# Revit family: SQN-D
name_source: partatom
category: Mechanical Equipment
revit_build: Autodesk Revit 2016 (Build: 20190507_1515(x64)
units: mm (PartAtom-declared; Revit-internal decimal feet)

## family parameters
Always vertical = Yes
Cut with Voids When Loaded = No
Part Type = Normal
Room Calculation Point = No
Round Connector Dimension = Use Diameter
Shared = No
Work Plane-Based = No

## types (46) — shared parameters
1.5 = 1 1/2"
FLANGE = 1"
HALF_F = 11 1/32"
HALF_G = 11 13/32"
LS = Yes
Manufacturer = Loren Cook Company
ONE EIGTH = 1/8"
T_SQ = 12"
T_SQ_HALF = 6"
URL = www.lorencook.com
ZERO = 0"

## per-type parameters (varying)
- 70_SQN-D: A_SUB=10"; B/2-VF_to_Side=2 13/16"; B_SUB=12"; B_SUB_MIN_.125=11 7/8"; C_SUB=14"; DEPTH=12"; D_PLUS_2=14"; D_SUB=12"; D_SUB_MINUS_.25=11 3/4"; D_SUB_TENTH=1 3/16"; E_SUB=13 9/16"; E_SUB_DIRECT=13 9/16"; FOURTH_B=3"; F_SUB=6 15/16"; G_SUB=6 1/8"; HALFC-B=1"; HALF_2H+D=7"; HALF_B=6"; HALF_B-G=2 15/16"; HALF_D=6"; HALF_D-A=1"; HALF_D-F=2 17/32"; HALF_D_SUB=6"; HALF_D_SUB_MIN_.25=5 7/8"; HALF_MP=2 3/32"; Height_with_VF=29 3/16"; INLET_RADIUS=3"; IN_RAD-D_SUB_TENTH=1 13/16"; IN_TENTH=1 13/16"; MOTOR_DEPTH=-8 3/4"; Model=SQN-D; NEGHALFC-B=-1"; NEG_HALF2H+D=-7"; NEG_HALF_D=-6"; PM=No; RAIL_SPACING=6"; SHAFT_RAD=1 1/8"; TENTHB+FOURTHB=-4 3/16"; TENTH_B=-1 3/16"; Type Comments=Centrifugal Square Inline Direct Drive; VF_to_Rear=2 1/8"; VF_to_Side=3 3/16"
- 90_SQN-D: A_SUB=12"; B/2-VF_to_Side=4 5/16"; B_SUB=15"; B_SUB_MIN_.125=14 7/8"; C_SUB=17"; DEPTH=15"; D_PLUS_2=16"; D_SUB=14"; D_SUB_MINUS_.25=13 3/4"; D_SUB_TENTH=1 13/32"; E_SUB=15 9/16"; E_SUB_DIRECT=15 9/16"; FOURTH_B=3 3/4"; F_SUB=8 15/16"; G_SUB=9 1/8"; HALFC-B=1"; HALF_2H+D=8"; HALF_B=7 1/2"; HALF_B-G=2 15/16"; HALF_D=7"; HALF_D-A=1"; HALF_D-F=2 17/32"; HALF_D_SUB=7"; HALF_D_SUB_MIN_.25=6 7/8"; HALF_MP=2 5/8"; Height_with_VF=29 3/16"; INLET_RADIUS=3 1/2"; IN_RAD-D_SUB_TENTH=2 3/32"; IN_TENTH=2 3/32"; MOTOR_DEPTH=-10 1/4"; Model=SQN-D; NEGHALFC-B=-1"; NEG_HALF2H+D=-8"; NEG_HALF_D=-7"; PM=No; RAIL_SPACING=7 1/2"; SHAFT_RAD=1 5/16"; TENTHB+FOURTHB=-5 1/4"; TENTH_B=-1 1/2"; Type Comments=Centrifugal Square Inline Direct Drive; VF_to_Rear=2 1/8"; VF_to_Side=3 3/16"
- 100_SQN-D: A_SUB=12"; B/2-VF_to_Side=6 13/16"; B_SUB=20"; B_SUB_MIN_.125=19 7/8"; C_SUB=22"; DEPTH=20"; D_PLUS_2=16"; D_SUB=14"; D_SUB_MINUS_.25=13 3/4"; D_SUB_TENTH=1 13/32"; E_SUB=12 1/2"; E_SUB_DIRECT=15 9/16"; FOURTH_B=5"; F_SUB=8 15/16"; G_SUB=14 1/8"; HALFC-B=1"; HALF_2H+D=8"; HALF_B=10"; HALF_B-G=2 15/16"; HALF_D=7"; HALF_D-A=1"; HALF_D-F=2 17/32"; HALF_D_SUB=7"; HALF_D_SUB_MIN_.25=6 7/8"; HALF_MP=3 1/2"; Height_with_VF=29 3/16"; INLET_RADIUS=3 1/2"; IN_RAD-D_SUB_TENTH=2 3/32"; IN_TENTH=2 3/32"; MOTOR_DEPTH=-12 3/4"; Model=SQN-D; NEGHALFC-B=-1"; NEG_HALF2H+D=-8"; NEG_HALF_D=-7"; PM=No; RAIL_SPACING=10"; SHAFT_RAD=1 1/32"; TENTHB+FOURTHB=-7"; TENTH_B=-2"; Type Comments=Centrifugal Square Inline Direct Drive; VF_to_Rear=2 1/8"; VF_to_Side=3 3/16"
- 120_SQN-D: A_SUB=16"; B/2-VF_to_Side=6 13/16"; B_SUB=20"; B_SUB_MIN_.125=19 7/8"; C_SUB=22"; DEPTH=20"; D_PLUS_2=20 7/16"; D_SUB=18 7/16"; D_SUB_MINUS_.25=18 3/16"; D_SUB_TENTH=1 27/32"; E_SUB=12 1/2"; E_SUB_DIRECT=20"; FOURTH_B=5"; F_SUB=12 9/16"; G_SUB=14 1/8"; HALFC-B=1"; HALF_2H+D=10 7/32"; HALF_B=10"; HALF_B-G=2 15/16"; HALF_D=9 7/32"; HALF_D-A=1 7/32"; HALF_D-F=2 15/16"; HALF_D_SUB=9 7/32"; HALF_D_SUB_MIN_.25=9 3/32"; HALF_MP=3 1/2"; Height_with_VF=29 3/16"; INLET_RADIUS=4 5/8"; IN_RAD-D_SUB_TENTH=2 25/32"; IN_TENTH=2 25/32"; MOTOR_DEPTH=-12 3/4"; Model=SQN-D; NEGHALFC-B=-1"; NEG_HALF2H+D=-10 7/32"; NEG_HALF_D=-9 7/32"; PM=No; RAIL_SPACING=10"; SHAFT_RAD=1 1/32"; TENTHB+FOURTHB=-7"; TENTH_B=-2"; Type Comments=Centrifugal Square Inline Direct Drive; VF_to_Rear=2 1/8"; VF_to_Side=3 3/16"
- 135_SQN-D: A_SUB=18"; B/2-VF_to_Side=6 15/16"; B_SUB=20 1/4"; B_SUB_MIN_.125=20 1/8"; C_SUB=22 1/4"; DEPTH=20 1/4"; D_PLUS_2=22 3/4"; D_SUB=20 3/4"; D_SUB_MINUS_.25=20 1/2"; D_SUB_TENTH=2 1/16"; E_SUB=12 1/2"; E_SUB_DIRECT=22 5/16"; FOURTH_B=5 1/16"; F_SUB=13 1/8"; G_SUB=14 1/4"; HALFC-B=1"; HALF_2H+D=11 3/8"; HALF_B=10 1/8"; HALF_B-G=3"; HALF_D=10 3/8"; HALF_D-A=1 3/8"; HALF_D-F=3 13/16"; HALF_D_SUB=10 3/8"; HALF_D_SUB_MIN_.25=10 1/4"; HALF_MP=3 17/32"; Height_with_VF=29 3/16"; INLET_RADIUS=5 3/16"; IN_RAD-D_SUB_TENTH=3 1/8"; IN_TENTH=3 1/8"; MOTOR_DEPTH=-12 7/8"; Model=SQN-D; NEGHALFC-B=-1"; NEG_HALF2H+D=-11 3/8"; NEG_HALF_D=-10 3/8"; PM=No; RAIL_SPACING=10 1/8"; SHAFT_RAD=1 1/32"; TENTHB+FOURTHB=-7 3/32"; TENTH_B=-2 1/32"; Type Comments=Centrifugal Square Inline Direct Drive; VF_to_Rear=2 1/8"; VF_to_Side=3 3/16"
- 150_SQN-D: A_SUB=20"; B/2-VF_to_Side=7 3/4"; B_SUB=21 7/8"; B_SUB_MIN_.125=21 3/4"; C_SUB=23 7/8"; DEPTH=21 7/8"; D_PLUS_2=25"; D_SUB=23"; D_SUB_MINUS_.25=22 3/4"; D_SUB_TENTH=2 5/16"; E_SUB=12 3/4"; E_SUB_DIRECT=25 1/16"; FOURTH_B=5 15/32"; F_SUB=16 1/8"; G_SUB=15 15/16"; HALFC-B=1"; HALF_2H+D=12 1/2"; HALF_B=10 15/16"; HALF_B-G=2 31/32"; HALF_D=11 1/2"; HALF_D-A=1 1/2"; HALF_D-F=3 7/16"; HALF_D_SUB=11 1/2"; HALF_D_SUB_MIN_.25=11 3/8"; HALF_MP=3 27/32"; Height_with_VF=29 3/16"; INLET_RADIUS=5 3/4"; IN_RAD-D_SUB_TENTH=3 7/16"; IN_TENTH=3 7/16"; MOTOR_DEPTH=-13 11/16"; Model=SQN-D; NEGHALFC-B=-1"; NEG_HALF2H+D=-12 1/2"; NEG_HALF_D=-11 1/2"; PM=No; RAIL_SPACING=10 15/16"; SHAFT_RAD=1 1/16"; TENTHB+FOURTHB=-7 21/32"; TENTH_B=-2 3/16"; Type Comments=Centrifugal Square Inline Direct Drive; VF_to_Rear=2 1/8"; VF_to_Side=3 3/16"
- 165_SQN-D: A_SUB=22"; B/2-VF_to_Side=9 5/16"; B_SUB=25"; B_SUB_MIN_.125=24 7/8"; C_SUB=27"; DEPTH=25"; D_PLUS_2=27 5/16"; D_SUB=25 5/16"; D_SUB_MINUS_.25=25 1/16"; D_SUB_TENTH=2 17/32"; E_SUB=14 3/4"; E_SUB_DIRECT=27 3/8"; FOURTH_B=6 1/4"; F_SUB=18 1/8"; G_SUB=19 1/8"; HALFC-B=1"; HALF_2H+D=13 21/32"; HALF_B=12 1/2"; HALF_B-G=2 15/16"; HALF_D=12 21/32"; HALF_D-A=1 21/32"; HALF_D-F=3 19/32"; HALF_D_SUB=12 21/32"; HALF_D_SUB_MIN_.25=12 17/32"; HALF_MP=4 3/8"; Height_with_VF=29 3/16"; INLET_RADIUS=6 11/32"; IN_RAD-D_SUB_TENTH=3 13/16"; IN_TENTH=3 13/16"; MOTOR_DEPTH=-15 1/4"; Model=SQN-D; NEGHALFC-B=-1"; NEG_HALF2H+D=-13 21/32"; NEG_HALF_D=-12 21/32"; PM=No; RAIL_SPACING=12 1/2"; SHAFT_RAD=1 7/32"; TENTHB+FOURTHB=-8 3/4"; TENTH_B=-2 1/2"; Type Comments=Centrifugal Square Inline Direct Drive; VF_to_Rear=2 1/8"; VF_to_Side=3 3/16"
- 120_SQN-D-VF: A_SUB=16"; B/2-VF_to_Side=6 13/16"; B_SUB=20"; B_SUB_MIN_.125=19 7/8"; C_SUB=22"; DEPTH=20"; D_PLUS_2=20 7/16"; D_SUB=18 7/16"; D_SUB_MINUS_.25=18 3/16"; D_SUB_TENTH=1 27/32"; E_SUB=12 1/2"; E_SUB_DIRECT=20"; FOURTH_B=5"; F_SUB=12 9/16"; G_SUB=14 1/8"; HALFC-B=1"; HALF_2H+D=10 7/32"; HALF_B=10"; HALF_B-G=2 15/16"; HALF_D=9 7/32"; HALF_D-A=1 7/32"; HALF_D-F=2 15/16"; HALF_D_SUB=9 7/32"; HALF_D_SUB_MIN_.25=9 3/32"; HALF_MP=3 1/2"; Height_with_VF=29 3/16"; INLET_RADIUS=4 5/8"; IN_RAD-D_SUB_TENTH=2 25/32"; IN_TENTH=2 25/32"; MOTOR_DEPTH=-12 3/4"; Model=SQN-D-VF; NEGHALFC-B=-1"; NEG_HALF2H+D=-10 7/32"; NEG_HALF_D=-9 7/32"; PM=No; RAIL_SPACING=10"; SHAFT_RAD=1 1/32"; TENTHB+FOURTHB=-7"; TENTH_B=-2"; Type Comments=Centrifugal Square Inline Direct Drive Preprogrammed EC Electronically Commutated Vari-Flow Motor; VF_to_Rear=2 1/8"; VF_to_Side=3 3/16"
- 135_SQN-D-VF: A_SUB=18"; B/2-VF_to_Side=5 3/4"; B_SUB=20 1/4"; B_SUB_MIN_.125=20 1/8"; C_SUB=22 1/4"; DEPTH=20 1/4"; D_PLUS_2=22 3/4"; D_SUB=20 3/4"; D_SUB_MINUS_.25=20 1/2"; D_SUB_TENTH=2 1/16"; E_SUB=12 1/2"; E_SUB_DIRECT=22 5/16"; FOURTH_B=5 1/16"; F_SUB=13 1/8"; G_SUB=14 1/4"; HALFC-B=1"; HALF_2H+D=11 3/8"; HALF_B=10 1/8"; HALF_B-G=3"; HALF_D=10 3/8"; HALF_D-A=1 3/8"; HALF_D-F=3 13/16"; HALF_D_SUB=10 3/8"; HALF_D_SUB_MIN_.25=10 1/4"; HALF_MP=3 17/32"; Height_with_VF=31 1/2"; INLET_RADIUS=5 3/16"; IN_RAD-D_SUB_TENTH=3 1/8"; IN_TENTH=3 1/8"; MOTOR_DEPTH=-12 7/8"; Model=SQN-D-VF; NEGHALFC-B=-1"; NEG_HALF2H+D=-11 3/8"; NEG_HALF_D=-10 3/8"; PM=No; RAIL_SPACING=10 1/8"; SHAFT_RAD=1 1/32"; TENTHB+FOURTHB=-7 3/32"; TENTH_B=-2 1/32"; Type Comments=Centrifugal Square Inline Direct Drive Preprogrammed EC Electronically Commutated Vari-Flow Motor; VF_to_Rear=8 1/8"; VF_to_Side=4 3/8"
- 150_SQN-D-VF: A_SUB=20"; B/2-VF_to_Side=5 7/16"; B_SUB=21 7/8"; B_SUB_MIN_.125=21 3/4"; C_SUB=23 7/8"; DEPTH=21 7/8"; D_PLUS_2=25"; D_SUB=23"; D_SUB_MINUS_.25=22 3/4"; D_SUB_TENTH=2 5/16"; E_SUB=12 3/4"; E_SUB_DIRECT=25 1/16"; FOURTH_B=5 15/32"; F_SUB=16 1/8"; G_SUB=15 15/16"; HALFC-B=1"; HALF_2H+D=12 1/2"; HALF_B=10 15/16"; HALF_B-G=2 31/32"; HALF_D=11 1/2"; HALF_D-A=1 1/2"; HALF_D-F=3 7/16"; HALF_D_SUB=11 1/2"; HALF_D_SUB_MIN_.25=11 3/8"; HALF_MP=3 27/32"; Height_with_VF=31 1/8"; INLET_RADIUS=5 3/4"; IN_RAD-D_SUB_TENTH=3 7/16"; IN_TENTH=3 7/16"; MOTOR_DEPTH=-13 11/16"; Model=SQN-D-VF; NEGHALFC-B=-1"; NEG_HALF2H+D=-12 1/2"; NEG_HALF_D=-11 1/2"; PM=No; RAIL_SPACING=10 15/16"; SHAFT_RAD=1 1/16"; TENTHB+FOURTHB=-7 21/32"; TENTH_B=-2 3/16"; Type Comments=Centrifugal Square Inline Direct Drive Preprogrammed EC Electronically Commutated Vari-Flow Motor; VF_to_Rear=11 3/4"; VF_to_Side=5 1/2"
- 165_SQN-D-VF: A_SUB=22"; B/2-VF_to_Side=5 7/8"; B_SUB=25"; B_SUB_MIN_.125=24 7/8"; C_SUB=27"; DEPTH=25"; D_PLUS_2=27 5/16"; D_SUB=25 5/16"; D_SUB_MINUS_.25=25 1/16"; D_SUB_TENTH=2 17/32"; E_SUB=14 3/4"; E_SUB_DIRECT=27 3/8"; FOURTH_B=6 1/4"; F_SUB=18 1/8"; G_SUB=19 1/8"; HALFC-B=1"; HALF_2H+D=13 21/32"; HALF_B=12 1/2"; HALF_B-G=2 15/16"; HALF_D=12 21/32"; HALF_D-A=1 21/32"; HALF_D-F=3 19/32"; HALF_D_SUB=12 21/32"; HALF_D_SUB_MIN_.25=12 17/32"; HALF_MP=4 3/8"; Height_with_VF=33 1/2"; INLET_RADIUS=6 11/32"; IN_RAD-D_SUB_TENTH=3 13/16"; IN_TENTH=3 13/16"; MOTOR_DEPTH=-15 1/4"; Model=SQN-D-VF; NEGHALFC-B=-1"; NEG_HALF2H+D=-13 21/32"; NEG_HALF_D=-12 21/32"; PM=No; RAIL_SPACING=12 1/2"; SHAFT_RAD=1 7/32"; TENTHB+FOURTHB=-8 3/4"; TENTH_B=-2 1/2"; Type Comments=Centrifugal Square Inline Direct Drive Preprogrammed EC Electronically Commutated Vari-Flow Motor; VF_to_Rear=13 7/8"; VF_to_Side=6 5/8"
- 120_SQN-D-VF2: A_SUB=16"; B/2-VF_to_Side=6 13/16"; B_SUB=20"; B_SUB_MIN_.125=19 7/8"; C_SUB=22"; DEPTH=20"; D_PLUS_2=20 7/16"; D_SUB=18 7/16"; D_SUB_MINUS_.25=18 3/16"; D_SUB_TENTH=1 27/32"; E_SUB=12 1/2"; E_SUB_DIRECT=20"; FOURTH_B=5"; F_SUB=12 9/16"; G_SUB=14 1/8"; HALFC-B=1"; HALF_2H+D=10 7/32"; HALF_B=10"; HALF_B-G=2 15/16"; HALF_D=9 7/32"; HALF_D-A=1 7/32"; HALF_D-F=2 15/16"; HALF_D_SUB=9 7/32"; HALF_D_SUB_MIN_.25=9 3/32"; HALF_MP=3 1/2"; Height_with_VF=29 3/16"; INLET_RADIUS=4 5/8"; IN_RAD-D_SUB_TENTH=2 25/32"; IN_TENTH=2 25/32"; MOTOR_DEPTH=-12 3/4"; Model=SQN-D-VF2; NEGHALFC-B=-1"; NEG_HALF2H+D=-10 7/32"; NEG_HALF_D=-9 7/32"; PM=Yes; RAIL_SPACING=10"; SHAFT_RAD=1 1/32"; TENTHB+FOURTHB=-7"; TENTH_B=-2"; Type Comments=Centrifugal Square Inline Direct Drive Preprogrammed PM Electronically Commutated Vari-Flow Motor; VF_to_Rear=2 1/8"; VF_to_Side=3 3/16"
- 135_SQN-D-VF2: A_SUB=18"; B/2-VF_to_Side=5 3/4"; B_SUB=20 1/4"; B_SUB_MIN_.125=20 1/8"; C_SUB=22 1/4"; DEPTH=20 1/4"; D_PLUS_2=22 3/4"; D_SUB=20 3/4"; D_SUB_MINUS_.25=20 1/2"; D_SUB_TENTH=2 1/16"; E_SUB=12 1/2"; E_SUB_DIRECT=22 5/16"; FOURTH_B=5 1/16"; F_SUB=13 1/8"; G_SUB=14 1/4"; HALFC-B=1"; HALF_2H+D=11 3/8"; HALF_B=10 1/8"; HALF_B-G=3"; HALF_D=10 3/8"; HALF_D-A=1 3/8"; HALF_D-F=3 13/16"; HALF_D_SUB=10 3/8"; HALF_D_SUB_MIN_.25=10 1/4"; HALF_MP=3 17/32"; Height_with_VF=31 1/2"; INLET_RADIUS=5 3/16"; IN_RAD-D_SUB_TENTH=3 1/8"; IN_TENTH=3 1/8"; MOTOR_DEPTH=-12 7/8"; Model=SQN-D-VF2; NEGHALFC-B=-1"; NEG_HALF2H+D=-11 3/8"; NEG_HALF_D=-10 3/8"; PM=Yes; RAIL_SPACING=10 1/8"; SHAFT_RAD=1 1/32"; TENTHB+FOURTHB=-7 3/32"; TENTH_B=-2 1/32"; Type Comments=Centrifugal Square Inline Direct Drive Preprogrammed PM Electronically Commutated Vari-Flow Motor; VF_to_Rear=8 1/8"; VF_to_Side=4 3/8"
- 150_SQN-D-VF2: A_SUB=20"; B/2-VF_to_Side=5 7/16"; B_SUB=21 7/8"; B_SUB_MIN_.125=21 3/4"; C_SUB=23 7/8"; DEPTH=21 7/8"; D_PLUS_2=25"; D_SUB=23"; D_SUB_MINUS_.25=22 3/4"; D_SUB_TENTH=2 5/16"; E_SUB=12 3/4"; E_SUB_DIRECT=25 1/16"; FOURTH_B=5 15/32"; F_SUB=16 1/8"; G_SUB=15 15/16"; HALFC-B=1"; HALF_2H+D=12 1/2"; HALF_B=10 15/16"; HALF_B-G=2 31/32"; HALF_D=11 1/2"; HALF_D-A=1 1/2"; HALF_D-F=3 7/16"; HALF_D_SUB=11 1/2"; HALF_D_SUB_MIN_.25=11 3/8"; HALF_MP=3 27/32"; Height_with_VF=31 1/8"; INLET_RADIUS=5 3/4"; IN_RAD-D_SUB_TENTH=3 7/16"; IN_TENTH=3 7/16"; MOTOR_DEPTH=-13 11/16"; Model=SQN-D-VF2; NEGHALFC-B=-1"; NEG_HALF2H+D=-12 1/2"; NEG_HALF_D=-11 1/2"; PM=Yes; RAIL_SPACING=10 15/16"; SHAFT_RAD=1 1/16"; TENTHB+FOURTHB=-7 21/32"; TENTH_B=-2 3/16"; Type Comments=Centrifugal Square Inline Direct Drive Preprogrammed PM Electronically Commutated Vari-Flow Motor; VF_to_Rear=11 3/4"; VF_to_Side=5 1/2"
- 165_SQN-D-VF2: A_SUB=22"; B/2-VF_to_Side=5 7/8"; B_SUB=25"; B_SUB_MIN_.125=24 7/8"; C_SUB=27"; DEPTH=25"; D_PLUS_2=27 5/16"; D_SUB=25 5/16"; D_SUB_MINUS_.25=25 1/16"; D_SUB_TENTH=2 17/32"; E_SUB=14 3/4"; E_SUB_DIRECT=27 3/8"; FOURTH_B=6 1/4"; F_SUB=18 1/8"; G_SUB=19 1/8"; HALFC-B=1"; HALF_2H+D=13 21/32"; HALF_B=12 1/2"; HALF_B-G=2 15/16"; HALF_D=12 21/32"; HALF_D-A=1 21/32"; HALF_D-F=3 19/32"; HALF_D_SUB=12 21/32"; HALF_D_SUB_MIN_.25=12 17/32"; HALF_MP=4 3/8"; Height_with_VF=33 1/2"; INLET_RADIUS=6 11/32"; IN_RAD-D_SUB_TENTH=3 13/16"; IN_TENTH=3 13/16"; MOTOR_DEPTH=-15 1/4"; Model=SQN-D-VF2; NEGHALFC-B=-1"; NEG_HALF2H+D=-13 21/32"; NEG_HALF_D=-12 21/32"; PM=Yes; RAIL_SPACING=12 1/2"; SHAFT_RAD=1 7/32"; TENTHB+FOURTHB=-8 3/4"; TENTH_B=-2 1/2"; Type Comments=Centrifugal Square Inline Direct Drive Preprogrammed PM Electronically Commutated Vari-Flow Motor; VF_to_Rear=13 7/8"; VF_to_Side=6 5/8"
- 180_SQN-D: A_SUB=24"; B/2-VF_to_Side=10 13/16"; B_SUB=28"; B_SUB_MIN_.125=27 7/8"; C_SUB=30"; DEPTH=28"; D_PLUS_2=29 5/8"; D_SUB=27 5/8"; D_SUB_MINUS_.25=27 3/8"; D_SUB_TENTH=2 3/4"; E_SUB=14 3/4"; E_SUB_DIRECT=30 1/8"; FOURTH_B=7"; F_SUB=18 1/8"; G_SUB=19 1/8"; HALFC-B=1"; HALF_2H+D=14 13/16"; HALF_B=14"; HALF_B-G=4 7/16"; HALF_D=13 13/16"; HALF_D-A=1 13/16"; HALF_D-F=4 3/4"; HALF_D_SUB=13 13/16"; HALF_D_SUB_MIN_.25=13 11/16"; HALF_MP=4 29/32"; Height_with_VF=40"; INLET_RADIUS=6 29/32"; IN_RAD-D_SUB_TENTH=4 5/32"; IN_TENTH=4 5/32"; MOTOR_DEPTH=-16 3/4"; Model=SQN-D; NEGHALFC-B=-1"; NEG_HALF2H+D=-14 13/16"; NEG_HALF_D=-13 13/16"; PM=No; RAIL_SPACING=14"; SHAFT_RAD=1 7/32"; TENTHB+FOURTHB=-9 13/16"; TENTH_B=-2 13/16"; Type Comments=Centrifugal Square Inline Direct Drive; VF_to_Rear=2 1/8"; VF_to_Side=3 3/16"
- 195_SQN-D: A_SUB=26"; B/2-VF_to_Side=11 15/16"; B_SUB=30 1/4"; B_SUB_MIN_.125=30 1/8"; C_SUB=32 1/4"; DEPTH=30 1/4"; D_PLUS_2=31 15/16"; D_SUB=29 15/16"; D_SUB_MINUS_.25=29 11/16"; D_SUB_TENTH=3"; E_SUB=14 3/4"; E_SUB_DIRECT=32 7/16"; FOURTH_B=7 9/16"; F_SUB=18 1/8"; G_SUB=19 1/8"; HALFC-B=1"; HALF_2H+D=15 31/32"; HALF_B=15 1/8"; HALF_B-G=5 9/16"; HALF_D=14 31/32"; HALF_D-A=1 31/32"; HALF_D-F=5 29/32"; HALF_D_SUB=14 31/32"; HALF_D_SUB_MIN_.25=14 27/32"; HALF_MP=5 9/32"; Height_with_VF=40"; INLET_RADIUS=7 1/2"; IN_RAD-D_SUB_TENTH=4 1/2"; IN_TENTH=4 1/2"; MOTOR_DEPTH=-17 7/8"; Model=SQN-D; NEGHALFC-B=-1"; NEG_HALF2H+D=-15 31/32"; NEG_HALF_D=-14 31/32"; PM=No; RAIL_SPACING=15 1/8"; SHAFT_RAD=1 7/32"; TENTHB+FOURTHB=-10 19/32"; TENTH_B=-3 1/32"; Type Comments=Centrifugal Square Inline Direct Drive; VF_to_Rear=2 1/8"; VF_to_Side=3 3/16"
- 210_SQN-D: A_SUB=28"; B/2-VF_to_Side=12 13/16"; B_SUB=32"; B_SUB_MIN_.125=31 7/8"; C_SUB=35"; DEPTH=32"; D_PLUS_2=33 1/4"; D_SUB=31 1/4"; D_SUB_MINUS_.25=31"; D_SUB_TENTH=3 1/8"; E_SUB=14 3/4"; E_SUB_DIRECT=33 3/4"; FOURTH_B=8"; F_SUB=18 1/8"; G_SUB=19 1/8"; HALFC-B=1 1/2"; HALF_2H+D=16 5/8"; HALF_B=16"; HALF_B-G=6 7/16"; HALF_D=15 5/8"; HALF_D-A=1 5/8"; HALF_D-F=6 9/16"; HALF_D_SUB=15 5/8"; HALF_D_SUB_MIN_.25=15 1/2"; HALF_MP=5 19/32"; Height_with_VF=40"; INLET_RADIUS=7 13/16"; IN_RAD-D_SUB_TENTH=4 11/16"; IN_TENTH=4 11/16"; MOTOR_DEPTH=-18 3/4"; Model=SQN-D; NEGHALFC-B=-1 1/2"; NEG_HALF2H+D=-16 5/8"; NEG_HALF_D=-15 5/8"; PM=No; RAIL_SPACING=16"; SHAFT_RAD=1 7/32"; TENTHB+FOURTHB=-11 3/16"; TENTH_B=-3 3/16"; Type Comments=Centrifugal Square Inline Direct Drive; VF_to_Rear=2 1/8"; VF_to_Side=3 3/16"
- 225_SQN-D: A_SUB=30"; B/2-VF_to_Side=13 15/16"; B_SUB=34 1/4"; B_SUB_MIN_.125=34 1/8"; C_SUB=37 1/4"; DEPTH=34 1/4"; D_PLUS_2=35 1/2"; D_SUB=33 1/2"; D_SUB_MINUS_.25=33 1/4"; D_SUB_TENTH=3 11/32"; E_SUB=14 3/4"; E_SUB_DIRECT=36"; FOURTH_B=8 9/16"; F_SUB=18 1/8"; G_SUB=19 1/8"; HALFC-B=1 1/2"; HALF_2H+D=17 3/4"; HALF_B=17 1/8"; HALF_B-G=7 9/16"; HALF_D=16 3/4"; HALF_D-A=1 3/4"; HALF_D-F=7 11/16"; HALF_D_SUB=16 3/4"; HALF_D_SUB_MIN_.25=16 5/8"; HALF_MP=6"; Height_with_VF=48"; INLET_RADIUS=8 3/8"; IN_RAD-D_SUB_TENTH=5 1/32"; IN_TENTH=5 1/32"; MOTOR_DEPTH=-19 7/8"; Model=SQN-D; NEGHALFC-B=-1 1/2"; NEG_HALF2H+D=-17 3/4"; NEG_HALF_D=-16 3/4"; PM=No; RAIL_SPACING=17 1/8"; SHAFT_RAD=1 7/32"; TENTHB+FOURTHB=-12"; TENTH_B=-3 7/16"; Type Comments=Centrifugal Square Inline Direct Drive; VF_to_Rear=2 1/8"; VF_to_Side=3 3/16"
- 245_SQN-D: A_SUB=33"; B/2-VF_to_Side=15 5/32"; B_SUB=36 11/16"; B_SUB_MIN_.125=36 9/16"; C_SUB=40 13/16"; DEPTH=36 11/16"; D_PLUS_2=38"; D_SUB=36"; D_SUB_MINUS_.25=35 3/4"; D_SUB_TENTH=3 19/32"; E_SUB=14 3/4"; E_SUB_DIRECT=38 1/2"; FOURTH_B=9 3/16"; F_SUB=18 1/8"; G_SUB=19 1/8"; HALFC-B=2 1/16"; HALF_2H+D=19"; HALF_B=18 11/32"; HALF_B-G=8 25/32"; HALF_D=18"; HALF_D-A=1 1/2"; HALF_D-F=8 15/16"; HALF_D_SUB=18"; HALF_D_SUB_MIN_.25=17 7/8"; HALF_MP=6 13/32"; Height_with_VF=48"; INLET_RADIUS=9"; IN_RAD-D_SUB_TENTH=5 13/32"; IN_TENTH=5 13/32"; MOTOR_DEPTH=-21 3/32"; Model=SQN-D; NEGHALFC-B=-2 1/16"; NEG_HALF2H+D=-19"; NEG_HALF_D=-18"; PM=No; RAIL_SPACING=18 11/32"; SHAFT_RAD=1 7/32"; TENTHB+FOURTHB=-12 27/32"; TENTH_B=-3 21/32"; Type Comments=Centrifugal Square Inline Direct Drive; VF_to_Rear=2 1/8"; VF_to_Side=3 3/16"
- 270_SQN-D: A_SUB=36 3/8"; B/2-VF_to_Side=17 5/16"; B_SUB=41"; B_SUB_MIN_.125=40 7/8"; C_SUB=45"; DEPTH=41"; D_PLUS_2=41 11/16"; D_SUB=39 11/16"; D_SUB_MINUS_.25=39 7/16"; D_SUB_TENTH=3 31/32"; E_SUB=14 3/4"; E_SUB_DIRECT=42 3/16"; FOURTH_B=10 1/4"; F_SUB=18 1/8"; G_SUB=19 1/8"; HALFC-B=2"; HALF_2H+D=20 27/32"; HALF_B=20 1/2"; HALF_B-G=10 15/16"; HALF_D=19 27/32"; HALF_D-A=1 21/32"; HALF_D-F=10 25/32"; HALF_D_SUB=19 27/32"; HALF_D_SUB_MIN_.25=19 23/32"; HALF_MP=7 3/16"; Height_with_VF=48"; INLET_RADIUS=9 15/16"; IN_RAD-D_SUB_TENTH=5 31/32"; IN_TENTH=5 31/32"; MOTOR_DEPTH=-23 1/4"; Model=SQN-D; NEGHALFC-B=-2"; NEG_HALF2H+D=-20 27/32"; NEG_HALF_D=-19 27/32"; PM=No; RAIL_SPACING=20 1/2"; SHAFT_RAD=1 7/32"; TENTHB+FOURTHB=-14 11/32"; TENTH_B=-4 3/32"; Type Comments=Centrifugal Square Inline Direct Drive; VF_to_Rear=2 1/8"; VF_to_Side=3 3/16"
- 300_SQN-D: A_SUB=40"; B/2-VF_to_Side=19 13/16"; B_SUB=46"; B_SUB_MIN_.125=45 7/8"; C_SUB=50"; DEPTH=46"; D_PLUS_2=46"; D_SUB=44"; D_SUB_MINUS_.25=43 3/4"; D_SUB_TENTH=4 13/32"; E_SUB=14 3/4"; E_SUB_DIRECT=46 1/2"; FOURTH_B=11 1/2"; F_SUB=18 1/8"; G_SUB=19 1/8"; HALFC-B=2"; HALF_2H+D=23"; HALF_B=23"; HALF_B-G=13 7/16"; HALF_D=22"; HALF_D-A=2"; HALF_D-F=12 15/16"; HALF_D_SUB=22"; HALF_D_SUB_MIN_.25=21 7/8"; HALF_MP=8 1/16"; Height_with_VF=58"; INLET_RADIUS=11"; IN_RAD-D_SUB_TENTH=6 19/32"; IN_TENTH=6 19/32"; MOTOR_DEPTH=-25 3/4"; Model=SQN-D; NEGHALFC-B=-2"; NEG_HALF2H+D=-23"; NEG_HALF_D=-22"; PM=No; RAIL_SPACING=23"; SHAFT_RAD=1 7/32"; TENTHB+FOURTHB=-16 3/32"; TENTH_B=-4 19/32"; Type Comments=Centrifugal Square Inline Direct Drive; VF_to_Rear=2 1/8"; VF_to_Side=3 3/16"
- 330_SQN-D: A_SUB=44"; B/2-VF_to_Side=22 5/16"; B_SUB=51"; B_SUB_MIN_.125=50 7/8"; C_SUB=55"; DEPTH=51"; D_PLUS_2=50 7/16"; D_SUB=48 7/16"; D_SUB_MINUS_.25=48 3/16"; D_SUB_TENTH=4 27/32"; E_SUB=14 3/4"; E_SUB_DIRECT=50 15/16"; FOURTH_B=12 3/4"; F_SUB=18 1/8"; G_SUB=19 1/8"; HALFC-B=2"; HALF_2H+D=25 7/32"; HALF_B=25 1/2"; HALF_B-G=15 15/16"; HALF_D=24 7/32"; HALF_D-A=2 7/32"; HALF_D-F=15 5/32"; HALF_D_SUB=24 7/32"; HALF_D_SUB_MIN_.25=24 3/32"; HALF_MP=8 15/16"; Height_with_VF=58"; INLET_RADIUS=12 1/8"; IN_RAD-D_SUB_TENTH=7 9/32"; IN_TENTH=7 9/32"; MOTOR_DEPTH=-28 1/4"; Model=SQN-D; NEGHALFC-B=-2"; NEG_HALF2H+D=-25 7/32"; NEG_HALF_D=-24 7/32"; PM=No; RAIL_SPACING=25 1/2"; SHAFT_RAD=1 7/32"; TENTHB+FOURTHB=-17 27/32"; TENTH_B=-5 3/32"; Type Comments=Centrifugal Square Inline Direct Drive; VF_to_Rear=2 1/8"; VF_to_Side=3 3/16"
- 365_SQN-D: A_SUB=46"; B/2-VF_to_Side=25 7/32"; B_SUB=56 13/16"; B_SUB_MIN_.125=56 11/16"; C_SUB=60 13/16"; DEPTH=56 13/16"; D_PLUS_2=52"; D_SUB=50"; D_SUB_MINUS_.25=49 3/4"; D_SUB_TENTH=5"; E_SUB=14 3/4"; E_SUB_DIRECT=55 1/2"; FOURTH_B=14 7/32"; F_SUB=18 1/8"; G_SUB=19 1/8"; HALFC-B=2"; HALF_2H+D=26"; HALF_B=28 13/32"; HALF_B-G=18 27/32"; HALF_D=25"; HALF_D-A=2"; HALF_D-F=15 15/16"; HALF_D_SUB=25"; HALF_D_SUB_MIN_.25=24 7/8"; HALF_MP=9 15/16"; Height_with_VF=58"; INLET_RADIUS=12 1/2"; IN_RAD-D_SUB_TENTH=7 1/2"; IN_TENTH=7 1/2"; MOTOR_DEPTH=-31 5/32"; Model=SQN-D; NEGHALFC-B=-2"; NEG_HALF2H+D=-26"; NEG_HALF_D=-25"; PM=No; RAIL_SPACING=28 13/32"; SHAFT_RAD=1 7/32"; TENTHB+FOURTHB=-19 7/8"; TENTH_B=-5 11/16"; Type Comments=Centrifugal Square Inline Direct Drive; VF_to_Rear=2 1/8"; VF_to_Side=3 3/16"
- 100_SQN-D-VF: A_SUB=12"; B/2-VF_to_Side=6 13/16"; B_SUB=20"; B_SUB_MIN_.125=19 7/8"; C_SUB=22"; DEPTH=20"; D_PLUS_2=16"; D_SUB=14"; D_SUB_MINUS_.25=13 3/4"; D_SUB_TENTH=1 13/32"; E_SUB=12 1/2"; E_SUB_DIRECT=15 9/16"; FOURTH_B=5"; F_SUB=8 15/16"; G_SUB=14 1/8"; HALFC-B=1"; HALF_2H+D=8"; HALF_B=10"; HALF_B-G=2 15/16"; HALF_D=7"; HALF_D-A=1"; HALF_D-F=2 17/32"; HALF_D_SUB=7"; HALF_D_SUB_MIN_.25=6 7/8"; HALF_MP=3 1/2"; Height_with_VF=29 3/16"; INLET_RADIUS=3 1/2"; IN_RAD-D_SUB_TENTH=2 3/32"; IN_TENTH=2 3/32"; MOTOR_DEPTH=-12 3/4"; Model=SQN-D-VF; NEGHALFC-B=-1"; NEG_HALF2H+D=-8"; NEG_HALF_D=-7"; PM=No; RAIL_SPACING=10"; SHAFT_RAD=1 1/32"; TENTHB+FOURTHB=-7"; TENTH_B=-2"; Type Comments=Centrifugal Square Inline Direct Drive Preprogrammed EC Electronically Commutated Vari-Flow Motor; VF_to_Rear=2 1/8"; VF_to_Side=3 3/16"
- 70_SQN-D-VF: A_SUB=10"; B/2-VF_to_Side=2 13/16"; B_SUB=12"; B_SUB_MIN_.125=11 7/8"; C_SUB=14"; DEPTH=12"; D_PLUS_2=14"; D_SUB=12"; D_SUB_MINUS_.25=11 3/4"; D_SUB_TENTH=1 3/16"; E_SUB=13 9/16"; E_SUB_DIRECT=13 9/16"; FOURTH_B=3"; F_SUB=6 15/16"; G_SUB=6 1/8"; HALFC-B=1"; HALF_2H+D=7"; HALF_B=6"; HALF_B-G=2 15/16"; HALF_D=6"; HALF_D-A=1"; HALF_D-F=2 17/32"; HALF_D_SUB=6"; HALF_D_SUB_MIN_.25=5 7/8"; HALF_MP=2 3/32"; Height_with_VF=29 3/16"; INLET_RADIUS=3"; IN_RAD-D_SUB_TENTH=1 13/16"; IN_TENTH=1 13/16"; MOTOR_DEPTH=-8 3/4"; Model=SQN-D-VF; NEGHALFC-B=-1"; NEG_HALF2H+D=-7"; NEG_HALF_D=-6"; PM=No; RAIL_SPACING=6"; SHAFT_RAD=1 1/8"; TENTHB+FOURTHB=-4 3/16"; TENTH_B=-1 3/16"; Type Comments=Centrifugal Square Inline Direct Drive Preprogrammed EC Electronically Commutated Vari-Flow Motor; VF_to_Rear=2 1/8"; VF_to_Side=3 3/16"
- 90_SQN-D-VF: A_SUB=12"; B/2-VF_to_Side=4 5/16"; B_SUB=15"; B_SUB_MIN_.125=14 7/8"; C_SUB=17"; DEPTH=15"; D_PLUS_2=16"; D_SUB=14"; D_SUB_MINUS_.25=13 3/4"; D_SUB_TENTH=1 13/32"; E_SUB=15 9/16"; E_SUB_DIRECT=15 9/16"; FOURTH_B=3 3/4"; F_SUB=8 15/16"; G_SUB=9 1/8"; HALFC-B=1"; HALF_2H+D=8"; HALF_B=7 1/2"; HALF_B-G=2 15/16"; HALF_D=7"; HALF_D-A=1"; HALF_D-F=2 17/32"; HALF_D_SUB=7"; HALF_D_SUB_MIN_.25=6 7/8"; HALF_MP=2 5/8"; Height_with_VF=29 3/16"; INLET_RADIUS=3 1/2"; IN_RAD-D_SUB_TENTH=2 3/32"; IN_TENTH=2 3/32"; MOTOR_DEPTH=-10 1/4"; Model=SQN-D-VF; NEGHALFC-B=-1"; NEG_HALF2H+D=-8"; NEG_HALF_D=-7"; PM=No; RAIL_SPACING=7 1/2"; SHAFT_RAD=1 5/16"; TENTHB+FOURTHB=-5 1/4"; TENTH_B=-1 1/2"; Type Comments=Centrifugal Square Inline Direct Drive Preprogrammed EC Electronically Commutated Vari-Flow Motor; VF_to_Rear=2 1/8"; VF_to_Side=3 3/16"
- 100_SQN-D-VF2: A_SUB=12"; B/2-VF_to_Side=6 13/16"; B_SUB=20"; B_SUB_MIN_.125=19 7/8"; C_SUB=22"; DEPTH=20"; D_PLUS_2=16"; D_SUB=14"; D_SUB_MINUS_.25=13 3/4"; D_SUB_TENTH=1 13/32"; E_SUB=12 1/2"; E_SUB_DIRECT=15 9/16"; FOURTH_B=5"; F_SUB=8 15/16"; G_SUB=14 1/8"; HALFC-B=1"; HALF_2H+D=8"; HALF_B=10"; HALF_B-G=2 15/16"; HALF_D=7"; HALF_D-A=1"; HALF_D-F=2 17/32"; HALF_D_SUB=7"; HALF_D_SUB_MIN_.25=6 7/8"; HALF_MP=3 1/2"; Height_with_VF=29 3/16"; INLET_RADIUS=3 1/2"; IN_RAD-D_SUB_TENTH=2 3/32"; IN_TENTH=2 3/32"; MOTOR_DEPTH=-12 3/4"; Model=SQN-D-VF2; NEGHALFC-B=-1"; NEG_HALF2H+D=-8"; NEG_HALF_D=-7"; PM=Yes; RAIL_SPACING=10"; SHAFT_RAD=1 1/32"; TENTHB+FOURTHB=-7"; TENTH_B=-2"; Type Comments=Centrifugal Square Inline Direct Drive Preprogrammed EC Electronically Commutated Vari-Flow Motor; VF_to_Rear=2 1/8"; VF_to_Side=3 3/16"
- 180_SQN-D_VF: A_SUB=24"; B/2-VF_to_Side=10 13/16"; B_SUB=28"; B_SUB_MIN_.125=27 7/8"; C_SUB=30"; DEPTH=28"; D_PLUS_2=29 5/8"; D_SUB=27 5/8"; D_SUB_MINUS_.25=27 3/8"; D_SUB_TENTH=2 3/4"; E_SUB=14 3/4"; E_SUB_DIRECT=30 1/8"; FOURTH_B=7"; F_SUB=18 1/8"; G_SUB=19 1/8"; HALFC-B=1"; HALF_2H+D=14 13/16"; HALF_B=14"; HALF_B-G=4 7/16"; HALF_D=13 13/16"; HALF_D-A=1 13/16"; HALF_D-F=4 3/4"; HALF_D_SUB=13 13/16"; HALF_D_SUB_MIN_.25=13 11/16"; HALF_MP=4 29/32"; Height_with_VF=40"; INLET_RADIUS=6 29/32"; IN_RAD-D_SUB_TENTH=4 5/32"; IN_TENTH=4 5/32"; MOTOR_DEPTH=-16 3/4"; Model=SQN-D-VF; NEGHALFC-B=-1"; NEG_HALF2H+D=-14 13/16"; NEG_HALF_D=-13 13/16"; PM=No; RAIL_SPACING=14"; SHAFT_RAD=1 7/32"; TENTHB+FOURTHB=-9 13/16"; TENTH_B=-2 13/16"; Type Comments=Centrifugal Square Inline Direct Drive Preprogrammed EC Electronically Commutated Vari-Flow Motor; VF_to_Rear=2 1/8"; VF_to_Side=3 3/16"
- 180_SQN-D-VF2: A_SUB=24"; B/2-VF_to_Side=10 13/16"; B_SUB=28"; B_SUB_MIN_.125=27 7/8"; C_SUB=30"; DEPTH=28"; D_PLUS_2=29 5/8"; D_SUB=27 5/8"; D_SUB_MINUS_.25=27 3/8"; D_SUB_TENTH=2 3/4"; E_SUB=14 3/4"; E_SUB_DIRECT=30 1/8"; FOURTH_B=7"; F_SUB=18 1/8"; G_SUB=19 1/8"; HALFC-B=1"; HALF_2H+D=14 13/16"; HALF_B=14"; HALF_B-G=4 7/16"; HALF_D=13 13/16"; HALF_D-A=1 13/16"; HALF_D-F=4 3/4"; HALF_D_SUB=13 13/16"; HALF_D_SUB_MIN_.25=13 11/16"; HALF_MP=4 29/32"; Height_with_VF=40"; INLET_RADIUS=6 29/32"; IN_RAD-D_SUB_TENTH=4 5/32"; IN_TENTH=4 5/32"; MOTOR_DEPTH=-16 3/4"; Model=SQN-D-VF2; NEGHALFC-B=-1"; NEG_HALF2H+D=-14 13/16"; NEG_HALF_D=-13 13/16"; PM=Yes; RAIL_SPACING=14"; SHAFT_RAD=1 7/32"; TENTHB+FOURTHB=-9 13/16"; TENTH_B=-2 13/16"; Type Comments=Centrifugal Square Inline Direct Drive Preprogrammed EC Electronically Commutated Vari-Flow Motor; VF_to_Rear=2 1/8"; VF_to_Side=3 3/16"
- 195_SQN-D-VF: A_SUB=26"; B/2-VF_to_Side=11 15/16"; B_SUB=30 1/4"; B_SUB_MIN_.125=30 1/8"; C_SUB=32 1/4"; DEPTH=30 1/4"; D_PLUS_2=31 15/16"; D_SUB=29 15/16"; D_SUB_MINUS_.25=29 11/16"; D_SUB_TENTH=3"; E_SUB=14 3/4"; E_SUB_DIRECT=32 7/16"; FOURTH_B=7 9/16"; F_SUB=18 1/8"; G_SUB=19 1/8"; HALFC-B=1"; HALF_2H+D=15 31/32"; HALF_B=15 1/8"; HALF_B-G=5 9/16"; HALF_D=14 31/32"; HALF_D-A=1 31/32"; HALF_D-F=5 29/32"; HALF_D_SUB=14 31/32"; HALF_D_SUB_MIN_.25=14 27/32"; HALF_MP=5 9/32"; Height_with_VF=40"; INLET_RADIUS=7 1/2"; IN_RAD-D_SUB_TENTH=4 1/2"; IN_TENTH=4 1/2"; MOTOR_DEPTH=-17 7/8"; Model=SQN-D-VF; NEGHALFC-B=-1"; NEG_HALF2H+D=-15 31/32"; NEG_HALF_D=-14 31/32"; PM=No; RAIL_SPACING=15 1/8"; SHAFT_RAD=1 7/32"; TENTHB+FOURTHB=-10 19/32"; TENTH_B=-3 1/32"; Type Comments=Centrifugal Square Inline Direct Drive Preprogrammed EC Electronically Commutated Vari-Flow Motor; VF_to_Rear=2 1/8"; VF_to_Side=3 3/16"
- 195_SQN-D-VF2: A_SUB=26"; B/2-VF_to_Side=11 15/16"; B_SUB=30 1/4"; B_SUB_MIN_.125=30 1/8"; C_SUB=32 1/4"; DEPTH=30 1/4"; D_PLUS_2=31 15/16"; D_SUB=29 15/16"; D_SUB_MINUS_.25=29 11/16"; D_SUB_TENTH=3"; E_SUB=14 3/4"; E_SUB_DIRECT=32 7/16"; FOURTH_B=7 9/16"; F_SUB=18 1/8"; G_SUB=19 1/8"; HALFC-B=1"; HALF_2H+D=15 31/32"; HALF_B=15 1/8"; HALF_B-G=5 9/16"; HALF_D=14 31/32"; HALF_D-A=1 31/32"; HALF_D-F=5 29/32"; HALF_D_SUB=14 31/32"; HALF_D_SUB_MIN_.25=14 27/32"; HALF_MP=5 9/32"; Height_with_VF=40"; INLET_RADIUS=7 1/2"; IN_RAD-D_SUB_TENTH=4 1/2"; IN_TENTH=4 1/2"; MOTOR_DEPTH=-17 7/8"; Model=SQN-D-VF2; NEGHALFC-B=-1"; NEG_HALF2H+D=-15 31/32"; NEG_HALF_D=-14 31/32"; PM=Yes; RAIL_SPACING=15 1/8"; SHAFT_RAD=1 7/32"; TENTHB+FOURTHB=-10 19/32"; TENTH_B=-3 1/32"; Type Comments=Centrifugal Square Inline Direct Drive Preprogrammed EC Electronically Commutated Vari-Flow Motor; VF_to_Rear=2 1/8"; VF_to_Side=3 3/16"
- 210_SQN-D-VF: A_SUB=28"; B/2-VF_to_Side=12 13/16"; B_SUB=32"; B_SUB_MIN_.125=31 7/8"; C_SUB=35"; DEPTH=32"; D_PLUS_2=33 1/4"; D_SUB=31 1/4"; D_SUB_MINUS_.25=31"; D_SUB_TENTH=3 1/8"; E_SUB=14 3/4"; E_SUB_DIRECT=33 3/4"; FOURTH_B=8"; F_SUB=18 1/8"; G_SUB=19 1/8"; HALFC-B=1 1/2"; HALF_2H+D=16 5/8"; HALF_B=16"; HALF_B-G=6 7/16"; HALF_D=15 5/8"; HALF_D-A=1 5/8"; HALF_D-F=6 9/16"; HALF_D_SUB=15 5/8"; HALF_D_SUB_MIN_.25=15 1/2"; HALF_MP=5 19/32"; Height_with_VF=40"; INLET_RADIUS=7 13/16"; IN_RAD-D_SUB_TENTH=4 11/16"; IN_TENTH=4 11/16"; MOTOR_DEPTH=-18 3/4"; Model=SQN-D-VF; NEGHALFC-B=-1 1/2"; NEG_HALF2H+D=-16 5/8"; NEG_HALF_D=-15 5/8"; PM=No; RAIL_SPACING=16"; SHAFT_RAD=1 7/32"; TENTHB+FOURTHB=-11 3/16"; TENTH_B=-3 3/16"; Type Comments=Centrifugal Square Inline Direct Drive Preprogrammed EC Electronically Commutated Vari-Flow Motor; VF_to_Rear=2 1/8"; VF_to_Side=3 3/16"
- 210_SQN-D-VF2: A_SUB=28"; B/2-VF_to_Side=12 13/16"; B_SUB=32"; B_SUB_MIN_.125=31 7/8"; C_SUB=35"; DEPTH=32"; D_PLUS_2=33 1/4"; D_SUB=31 1/4"; D_SUB_MINUS_.25=31"; D_SUB_TENTH=3 1/8"; E_SUB=14 3/4"; E_SUB_DIRECT=33 3/4"; FOURTH_B=8"; F_SUB=18 1/8"; G_SUB=19 1/8"; HALFC-B=1 1/2"; HALF_2H+D=16 5/8"; HALF_B=16"; HALF_B-G=6 7/16"; HALF_D=15 5/8"; HALF_D-A=1 5/8"; HALF_D-F=6 9/16"; HALF_D_SUB=15 5/8"; HALF_D_SUB_MIN_.25=15 1/2"; HALF_MP=5 19/32"; Height_with_VF=40"; INLET_RADIUS=7 13/16"; IN_RAD-D_SUB_TENTH=4 11/16"; IN_TENTH=4 11/16"; MOTOR_DEPTH=-18 3/4"; Model=SQN-D-VF2; NEGHALFC-B=-1 1/2"; NEG_HALF2H+D=-16 5/8"; NEG_HALF_D=-15 5/8"; PM=Yes; RAIL_SPACING=16"; SHAFT_RAD=1 7/32"; TENTHB+FOURTHB=-11 3/16"; TENTH_B=-3 3/16"; Type Comments=Centrifugal Square Inline Direct Drive Preprogrammed EC Electronically Commutated Vari-Flow Motor; VF_to_Rear=2 1/8"; VF_to_Side=3 3/16"
- 225_SQN-D-VF: A_SUB=30"; B/2-VF_to_Side=13 15/16"; B_SUB=34 1/4"; B_SUB_MIN_.125=34 1/8"; C_SUB=37 1/4"; DEPTH=34 1/4"; D_PLUS_2=35 1/2"; D_SUB=33 1/2"; D_SUB_MINUS_.25=33 1/4"; D_SUB_TENTH=3 11/32"; E_SUB=14 3/4"; E_SUB_DIRECT=36"; FOURTH_B=8 9/16"; F_SUB=18 1/8"; G_SUB=19 1/8"; HALFC-B=1 1/2"; HALF_2H+D=17 3/4"; HALF_B=17 1/8"; HALF_B-G=7 9/16"; HALF_D=16 3/4"; HALF_D-A=1 3/4"; HALF_D-F=7 11/16"; HALF_D_SUB=16 3/4"; HALF_D_SUB_MIN_.25=16 5/8"; HALF_MP=6"; Height_with_VF=48"; INLET_RADIUS=8 3/8"; IN_RAD-D_SUB_TENTH=5 1/32"; IN_TENTH=5 1/32"; MOTOR_DEPTH=-19 7/8"; Model=SQN-D-VF; NEGHALFC-B=-1 1/2"; NEG_HALF2H+D=-17 3/4"; NEG_HALF_D=-16 3/4"; PM=No; RAIL_SPACING=17 1/8"; SHAFT_RAD=1 7/32"; TENTHB+FOURTHB=-12"; TENTH_B=-3 7/16"; Type Comments=Centrifugal Square Inline Direct Drive Preprogrammed EC Electronically Commutated Vari-Flow Motor; VF_to_Rear=2 1/8"; VF_to_Side=3 3/16"
- 225_SQN-D-VF2: A_SUB=30"; B/2-VF_to_Side=13 15/16"; B_SUB=34 1/4"; B_SUB_MIN_.125=34 1/8"; C_SUB=37 1/4"; DEPTH=34 1/4"; D_PLUS_2=35 1/2"; D_SUB=33 1/2"; D_SUB_MINUS_.25=33 1/4"; D_SUB_TENTH=3 11/32"; E_SUB=14 3/4"; E_SUB_DIRECT=36"; FOURTH_B=8 9/16"; F_SUB=18 1/8"; G_SUB=19 1/8"; HALFC-B=1 1/2"; HALF_2H+D=17 3/4"; HALF_B=17 1/8"; HALF_B-G=7 9/16"; HALF_D=16 3/4"; HALF_D-A=1 3/4"; HALF_D-F=7 11/16"; HALF_D_SUB=16 3/4"; HALF_D_SUB_MIN_.25=16 5/8"; HALF_MP=6"; Height_with_VF=48"; INLET_RADIUS=8 3/8"; IN_RAD-D_SUB_TENTH=5 1/32"; IN_TENTH=5 1/32"; MOTOR_DEPTH=-19 7/8"; Model=SQN-D-VF2; NEGHALFC-B=-1 1/2"; NEG_HALF2H+D=-17 3/4"; NEG_HALF_D=-16 3/4"; PM=Yes; RAIL_SPACING=17 1/8"; SHAFT_RAD=1 7/32"; TENTHB+FOURTHB=-12"; TENTH_B=-3 7/16"; Type Comments=Centrifugal Square Inline Direct Drive Preprogrammed EC Electronically Commutated Vari-Flow Motor; VF_to_Rear=2 1/8"; VF_to_Side=3 3/16"
- 245_SQN-D-VF: A_SUB=33"; B/2-VF_to_Side=15 5/32"; B_SUB=36 11/16"; B_SUB_MIN_.125=36 9/16"; C_SUB=40 13/16"; DEPTH=36 11/16"; D_PLUS_2=38"; D_SUB=36"; D_SUB_MINUS_.25=35 3/4"; D_SUB_TENTH=3 19/32"; E_SUB=14 3/4"; E_SUB_DIRECT=38 1/2"; FOURTH_B=9 3/16"; F_SUB=18 1/8"; G_SUB=19 1/8"; HALFC-B=2 1/16"; HALF_2H+D=19"; HALF_B=18 11/32"; HALF_B-G=8 25/32"; HALF_D=18"; HALF_D-A=1 1/2"; HALF_D-F=8 15/16"; HALF_D_SUB=18"; HALF_D_SUB_MIN_.25=17 7/8"; HALF_MP=6 13/32"; Height_with_VF=48"; INLET_RADIUS=9"; IN_RAD-D_SUB_TENTH=5 13/32"; IN_TENTH=5 13/32"; MOTOR_DEPTH=-21 3/32"; Model=SQN-D-VF; NEGHALFC-B=-2 1/16"; NEG_HALF2H+D=-19"; NEG_HALF_D=-18"; PM=No; RAIL_SPACING=18 11/32"; SHAFT_RAD=1 7/32"; TENTHB+FOURTHB=-12 27/32"; TENTH_B=-3 21/32"; Type Comments=Centrifugal Square Inline Direct Drive Preprogrammed EC Electronically Commutated Vari-Flow Motor; VF_to_Rear=2 1/8"; VF_to_Side=3 3/16"
- 245_SQN-D-VF2: A_SUB=33"; B/2-VF_to_Side=15 5/32"; B_SUB=36 11/16"; B_SUB_MIN_.125=36 9/16"; C_SUB=40 13/16"; DEPTH=36 11/16"; D_PLUS_2=38"; D_SUB=36"; D_SUB_MINUS_.25=35 3/4"; D_SUB_TENTH=3 19/32"; E_SUB=14 3/4"; E_SUB_DIRECT=38 1/2"; FOURTH_B=9 3/16"; F_SUB=18 1/8"; G_SUB=19 1/8"; HALFC-B=2 1/16"; HALF_2H+D=19"; HALF_B=18 11/32"; HALF_B-G=8 25/32"; HALF_D=18"; HALF_D-A=1 1/2"; HALF_D-F=8 15/16"; HALF_D_SUB=18"; HALF_D_SUB_MIN_.25=17 7/8"; HALF_MP=6 13/32"; Height_with_VF=48"; INLET_RADIUS=9"; IN_RAD-D_SUB_TENTH=5 13/32"; IN_TENTH=5 13/32"; MOTOR_DEPTH=-21 3/32"; Model=SQN-D-VF2; NEGHALFC-B=-2 1/16"; NEG_HALF2H+D=-19"; NEG_HALF_D=-18"; PM=Yes; RAIL_SPACING=18 11/32"; SHAFT_RAD=1 7/32"; TENTHB+FOURTHB=-12 27/32"; TENTH_B=-3 21/32"; Type Comments=Centrifugal Square Inline Direct Drive Preprogrammed EC Electronically Commutated Vari-Flow Motor; VF_to_Rear=2 1/8"; VF_to_Side=3 3/16"
- 270_SQN-D-VF: A_SUB=36 3/8"; B/2-VF_to_Side=17 5/16"; B_SUB=41"; B_SUB_MIN_.125=40 7/8"; C_SUB=45"; DEPTH=41"; D_PLUS_2=41 11/16"; D_SUB=39 11/16"; D_SUB_MINUS_.25=39 7/16"; D_SUB_TENTH=3 31/32"; E_SUB=14 3/4"; E_SUB_DIRECT=42 3/16"; FOURTH_B=10 1/4"; F_SUB=18 1/8"; G_SUB=19 1/8"; HALFC-B=2"; HALF_2H+D=20 27/32"; HALF_B=20 1/2"; HALF_B-G=10 15/16"; HALF_D=19 27/32"; HALF_D-A=1 21/32"; HALF_D-F=10 25/32"; HALF_D_SUB=19 27/32"; HALF_D_SUB_MIN_.25=19 23/32"; HALF_MP=7 3/16"; Height_with_VF=48"; INLET_RADIUS=9 15/16"; IN_RAD-D_SUB_TENTH=5 31/32"; IN_TENTH=5 31/32"; MOTOR_DEPTH=-23 1/4"; Model=SQN-D-VF; NEGHALFC-B=-2"; NEG_HALF2H+D=-20 27/32"; NEG_HALF_D=-19 27/32"; PM=No; RAIL_SPACING=20 1/2"; SHAFT_RAD=1 7/32"; TENTHB+FOURTHB=-14 11/32"; TENTH_B=-4 3/32"; Type Comments=Centrifugal Square Inline Direct Drive Preprogrammed EC Electronically Commutated Vari-Flow Motor; VF_to_Rear=2 1/8"; VF_to_Side=3 3/16"
- 270_SQN-D-VF2: A_SUB=36 3/8"; B/2-VF_to_Side=17 5/16"; B_SUB=41"; B_SUB_MIN_.125=40 7/8"; C_SUB=45"; DEPTH=41"; D_PLUS_2=41 11/16"; D_SUB=39 11/16"; D_SUB_MINUS_.25=39 7/16"; D_SUB_TENTH=3 31/32"; E_SUB=14 3/4"; E_SUB_DIRECT=42 3/16"; FOURTH_B=10 1/4"; F_SUB=18 1/8"; G_SUB=19 1/8"; HALFC-B=2"; HALF_2H+D=20 27/32"; HALF_B=20 1/2"; HALF_B-G=10 15/16"; HALF_D=19 27/32"; HALF_D-A=1 21/32"; HALF_D-F=10 25/32"; HALF_D_SUB=19 27/32"; HALF_D_SUB_MIN_.25=19 23/32"; HALF_MP=7 3/16"; Height_with_VF=48"; INLET_RADIUS=9 15/16"; IN_RAD-D_SUB_TENTH=5 31/32"; IN_TENTH=5 31/32"; MOTOR_DEPTH=-23 1/4"; Model=SQN-D-VF2; NEGHALFC-B=-2"; NEG_HALF2H+D=-20 27/32"; NEG_HALF_D=-19 27/32"; PM=Yes; RAIL_SPACING=20 1/2"; SHAFT_RAD=1 7/32"; TENTHB+FOURTHB=-14 11/32"; TENTH_B=-4 3/32"; Type Comments=Centrifugal Square Inline Direct Drive Preprogrammed EC Electronically Commutated Vari-Flow Motor; VF_to_Rear=2 1/8"; VF_to_Side=3 3/16"
- 300_SQN-D-VF: A_SUB=40"; B/2-VF_to_Side=19 13/16"; B_SUB=46"; B_SUB_MIN_.125=45 7/8"; C_SUB=50"; DEPTH=46"; D_PLUS_2=46"; D_SUB=44"; D_SUB_MINUS_.25=43 3/4"; D_SUB_TENTH=4 13/32"; E_SUB=14 3/4"; E_SUB_DIRECT=46 1/2"; FOURTH_B=11 1/2"; F_SUB=18 1/8"; G_SUB=19 1/8"; HALFC-B=2"; HALF_2H+D=23"; HALF_B=23"; HALF_B-G=13 7/16"; HALF_D=22"; HALF_D-A=2"; HALF_D-F=12 15/16"; HALF_D_SUB=22"; HALF_D_SUB_MIN_.25=21 7/8"; HALF_MP=8 1/16"; Height_with_VF=58"; INLET_RADIUS=11"; IN_RAD-D_SUB_TENTH=6 19/32"; IN_TENTH=6 19/32"; MOTOR_DEPTH=-25 3/4"; Model=SQN-D-VF; NEGHALFC-B=-2"; NEG_HALF2H+D=-23"; NEG_HALF_D=-22"; PM=No; RAIL_SPACING=23"; SHAFT_RAD=1 7/32"; TENTHB+FOURTHB=-16 3/32"; TENTH_B=-4 19/32"; Type Comments=Centrifugal Square Inline Direct Drive Preprogrammed EC Electronically Commutated Vari-Flow Motor; VF_to_Rear=2 1/8"; VF_to_Side=3 3/16"
- 300_SQN-D-VF2: A_SUB=40"; B/2-VF_to_Side=19 13/16"; B_SUB=46"; B_SUB_MIN_.125=45 7/8"; C_SUB=50"; DEPTH=46"; D_PLUS_2=46"; D_SUB=44"; D_SUB_MINUS_.25=43 3/4"; D_SUB_TENTH=4 13/32"; E_SUB=14 3/4"; E_SUB_DIRECT=46 1/2"; FOURTH_B=11 1/2"; F_SUB=18 1/8"; G_SUB=19 1/8"; HALFC-B=2"; HALF_2H+D=23"; HALF_B=23"; HALF_B-G=13 7/16"; HALF_D=22"; HALF_D-A=2"; HALF_D-F=12 15/16"; HALF_D_SUB=22"; HALF_D_SUB_MIN_.25=21 7/8"; HALF_MP=8 1/16"; Height_with_VF=58"; INLET_RADIUS=11"; IN_RAD-D_SUB_TENTH=6 19/32"; IN_TENTH=6 19/32"; MOTOR_DEPTH=-25 3/4"; Model=SQN-D-VF2; NEGHALFC-B=-2"; NEG_HALF2H+D=-23"; NEG_HALF_D=-22"; PM=Yes; RAIL_SPACING=23"; SHAFT_RAD=1 7/32"; TENTHB+FOURTHB=-16 3/32"; TENTH_B=-4 19/32"; Type Comments=Centrifugal Square Inline Direct Drive Preprogrammed EC Electronically Commutated Vari-Flow Motor; VF_to_Rear=2 1/8"; VF_to_Side=3 3/16"
- 330_SQN-D-VF: A_SUB=44"; B/2-VF_to_Side=22 5/16"; B_SUB=51"; B_SUB_MIN_.125=50 7/8"; C_SUB=55"; DEPTH=51"; D_PLUS_2=50 7/16"; D_SUB=48 7/16"; D_SUB_MINUS_.25=48 3/16"; D_SUB_TENTH=4 27/32"; E_SUB=14 3/4"; E_SUB_DIRECT=50 15/16"; FOURTH_B=12 3/4"; F_SUB=18 1/8"; G_SUB=19 1/8"; HALFC-B=2"; HALF_2H+D=25 7/32"; HALF_B=25 1/2"; HALF_B-G=15 15/16"; HALF_D=24 7/32"; HALF_D-A=2 7/32"; HALF_D-F=15 5/32"; HALF_D_SUB=24 7/32"; HALF_D_SUB_MIN_.25=24 3/32"; HALF_MP=8 15/16"; Height_with_VF=58"; INLET_RADIUS=12 1/8"; IN_RAD-D_SUB_TENTH=7 9/32"; IN_TENTH=7 9/32"; MOTOR_DEPTH=-28 1/4"; Model=SQN-D-VF; NEGHALFC-B=-2"; NEG_HALF2H+D=-25 7/32"; NEG_HALF_D=-24 7/32"; PM=No; RAIL_SPACING=25 1/2"; SHAFT_RAD=1 7/32"; TENTHB+FOURTHB=-17 27/32"; TENTH_B=-5 3/32"; Type Comments=Centrifugal Square Inline Direct Drive Preprogrammed EC Electronically Commutated Vari-Flow Motor; VF_to_Rear=2 1/8"; VF_to_Side=3 3/16"
- 330_SQN-D-VF2: A_SUB=44"; B/2-VF_to_Side=22 5/16"; B_SUB=51"; B_SUB_MIN_.125=50 7/8"; C_SUB=55"; DEPTH=51"; D_PLUS_2=50 7/16"; D_SUB=48 7/16"; D_SUB_MINUS_.25=48 3/16"; D_SUB_TENTH=4 27/32"; E_SUB=14 3/4"; E_SUB_DIRECT=50 15/16"; FOURTH_B=12 3/4"; F_SUB=18 1/8"; G_SUB=19 1/8"; HALFC-B=2"; HALF_2H+D=25 7/32"; HALF_B=25 1/2"; HALF_B-G=15 15/16"; HALF_D=24 7/32"; HALF_D-A=2 7/32"; HALF_D-F=15 5/32"; HALF_D_SUB=24 7/32"; HALF_D_SUB_MIN_.25=24 3/32"; HALF_MP=8 15/16"; Height_with_VF=58"; INLET_RADIUS=12 1/8"; IN_RAD-D_SUB_TENTH=7 9/32"; IN_TENTH=7 9/32"; MOTOR_DEPTH=-28 1/4"; Model=SQN-D-VF2; NEGHALFC-B=-2"; NEG_HALF2H+D=-25 7/32"; NEG_HALF_D=-24 7/32"; PM=Yes; RAIL_SPACING=25 1/2"; SHAFT_RAD=1 7/32"; TENTHB+FOURTHB=-17 27/32"; TENTH_B=-5 3/32"; Type Comments=Centrifugal Square Inline Direct Drive Preprogrammed EC Electronically Commutated Vari-Flow Motor; VF_to_Rear=2 1/8"; VF_to_Side=3 3/16"
- 365_SQN-D-VF: A_SUB=46"; B/2-VF_to_Side=25 7/32"; B_SUB=56 13/16"; B_SUB_MIN_.125=56 11/16"; C_SUB=60 13/16"; DEPTH=56 13/16"; D_PLUS_2=52"; D_SUB=50"; D_SUB_MINUS_.25=49 3/4"; D_SUB_TENTH=5"; E_SUB=14 3/4"; E_SUB_DIRECT=55 1/2"; FOURTH_B=14 7/32"; F_SUB=18 1/8"; G_SUB=19 1/8"; HALFC-B=2"; HALF_2H+D=26"; HALF_B=28 13/32"; HALF_B-G=18 27/32"; HALF_D=25"; HALF_D-A=2"; HALF_D-F=15 15/16"; HALF_D_SUB=25"; HALF_D_SUB_MIN_.25=24 7/8"; HALF_MP=9 15/16"; Height_with_VF=58"; INLET_RADIUS=12 1/2"; IN_RAD-D_SUB_TENTH=7 1/2"; IN_TENTH=7 1/2"; MOTOR_DEPTH=-31 5/32"; Model=SQN-D-VF; NEGHALFC-B=-2"; NEG_HALF2H+D=-26"; NEG_HALF_D=-25"; PM=No; RAIL_SPACING=28 13/32"; SHAFT_RAD=1 7/32"; TENTHB+FOURTHB=-19 7/8"; TENTH_B=-5 11/16"; Type Comments=Centrifugal Square Inline Direct Drive Preprogrammed EC Electronically Commutated Vari-Flow Motor; VF_to_Rear=2 1/8"; VF_to_Side=3 3/16"
- 365_SQN-D-VF2: A_SUB=46"; B/2-VF_to_Side=25 7/32"; B_SUB=56 13/16"; B_SUB_MIN_.125=56 11/16"; C_SUB=60 13/16"; DEPTH=56 13/16"; D_PLUS_2=52"; D_SUB=50"; D_SUB_MINUS_.25=49 3/4"; D_SUB_TENTH=5"; E_SUB=14 3/4"; E_SUB_DIRECT=55 1/2"; FOURTH_B=14 7/32"; F_SUB=18 1/8"; G_SUB=19 1/8"; HALFC-B=2"; HALF_2H+D=26"; HALF_B=28 13/32"; HALF_B-G=18 27/32"; HALF_D=25"; HALF_D-A=2"; HALF_D-F=15 15/16"; HALF_D_SUB=25"; HALF_D_SUB_MIN_.25=24 7/8"; HALF_MP=9 15/16"; Height_with_VF=58"; INLET_RADIUS=12 1/2"; IN_RAD-D_SUB_TENTH=7 1/2"; IN_TENTH=7 1/2"; MOTOR_DEPTH=-31 5/32"; Model=SQN-D-VF2; NEGHALFC-B=-2"; NEG_HALF2H+D=-26"; NEG_HALF_D=-25"; PM=Yes; RAIL_SPACING=28 13/32"; SHAFT_RAD=1 7/32"; TENTHB+FOURTHB=-19 7/8"; TENTH_B=-5 11/16"; Type Comments=Centrifugal Square Inline Direct Drive Preprogrammed EC Electronically Commutated Vari-Flow Motor; VF_to_Rear=2 1/8"; VF_to_Side=3 3/16"

## geometry (parser evidence)
native form markers: Sweep x2
no freeform markers — native parametric forms only
